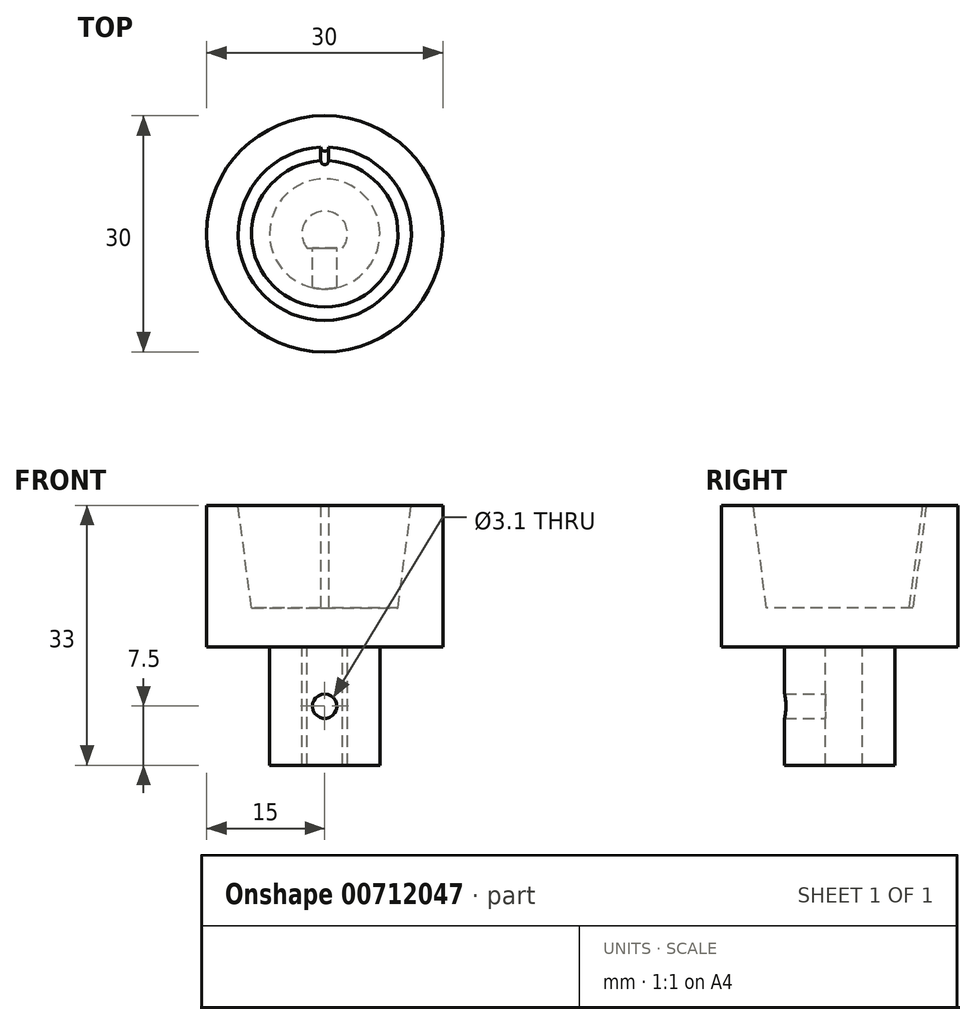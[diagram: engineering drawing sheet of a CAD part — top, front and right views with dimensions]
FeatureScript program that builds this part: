
annotation { "Feature Type Name" : "Feature", "Feature Type Description" : "" }
export const myFeature = defineFeature(function(context is Context, id is Id, definition is map)
    precondition{}
    {
        {
            var Q0;
            Q0=qCreatedBy(makeId("Top.planeOp"),FACE);
            var sketch = newSketch(context, id + "F0", { "sketchPlane" : qUnion([Q0])});
            skLineSegment(sketch, "E0", {"start": v(-2.27, -1.8) * mm, "end": v(2.27, -1.8) * mm});
            skArc(sketch, "E1", {"start": v(-2.27, -1.8) * mm, "mid": v(0, 2.9) * mm, "end": v(2.27, -1.8) * mm});
            skCircle(sketch, "E2", {"center": v(0, 0) * mm, "radius": 7 * mm});
            skCircle(sketch, "E3", {"center": v(0, 0) * mm, "radius": 10 * mm});
            skSolve(sketch);
        }
        {
            var Q0;
            Q0=makeQuery(id+"F0.imprint","IMPRINT",FACE,{"disambiguationData":[TD([[makeQuery(id+"F0.imprint","IMPRINT",EDGE,{"derivedFrom":sQuery(id+"F0.wireOp",EDGE,"E0")}),-1.0]])]});
            extrude(context, id + "F1", {"entities" : qUnion([Q0]), "oppositeDirection" : true, "depth" : 15 * mm, "offsetDistance" : 25 * mm});
        }
        {
            var Q0;
            Q0=makeQuery(id+"F0.imprint","IMPRINT",FACE,{"disambiguationData":[TD([[makeQuery(id+"F0.imprint","IMPRINT",EDGE,{"derivedFrom":sQuery(id+"F0.wireOp",EDGE,"E0")}),1.0]])]});
            var Q1;
            Q1=makeQuery(id+"F0.imprint","IMPRINT",FACE,{"disambiguationData":[TD([[makeQuery(id+"F0.imprint","IMPRINT",EDGE,{"derivedFrom":sQuery(id+"F0.wireOp",EDGE,"E0")}),-1.0]])]});
            var Q2;
            Q2=makeQuery(id+"F0.imprint","IMPRINT",FACE,{"disambiguationData":[TD([[makeQuery(id+"F0.imprint","IMPRINT",EDGE,{"derivedFrom":sQuery(id+"F0.wireOp",EDGE,"E2")}),-1.0]])]});
            extrude(context, id + "F2", {"entities" : qUnion([Q0, Q1, Q2]), "operationType" : NewBodyOperationType.ADD, "depth" : 5 * mm, "offsetDistance" : 25 * mm});
        }
        {
            var Q0;
            Q0=qCreatedBy(makeId("Right.planeOp"),FACE);
            var sketch = newSketch(context, id + "F3", { "sketchPlane" : qUnion([Q0])});
            skLineSegment(sketch, "E4", {"start": v(9.3, 0) * mm, "end": v(15, 0) * mm});
            skLineSegment(sketch, "E5", {"start": v(15, 0) * mm, "end": v(15, 18) * mm});
            skPoint(sketch, "E6.endSnap0", {"position": v(12.15, 0) * mm});
            skLineSegment(sketch, "E7", {"start": v(9.3, 5) * mm, "end": v(9.3, 0) * mm});
            skLineSegment(sketch, "E8", {"start": v(0, 0) * mm, "end": v(0, 7.26) * mm, "construction": true});
            skLineSegment(sketch, "E9", {"start": v(15, 18) * mm, "end": v(11, 18) * mm});
            skLineSegment(sketch, "E10", {"start": v(11, 18) * mm, "end": v(9.3, 5) * mm});
            skSolve(sketch);
        }
        {
            var Q0;
            Q0=makeQuery(id+"F3.imprint","IMPRINT",FACE,{"disambiguationData":[TD([[makeQuery(id+"F3.imprint","IMPRINT",EDGE,{"derivedFrom":sQuery(id+"F3.wireOp",EDGE,"E4")}),1.0]])]});
            var Q1;
            Q1=sQuery(id+"F3.wireOp",EDGE,"E8");
            revolve(context, id + "F4", {"operationType" : NewBodyOperationType.ADD, "surfaceOperationType" : NewSurfaceOperationType.NEW, "entities" : qUnion([Q0]), "axis" : qUnion([Q1]), "revolveType" : RevolveType.FULL});
        }
        {
            var Q0;
            Q0=makeQuery(id+"F1.opExtrude","SWEPT_FACE",FACE,{"disambiguationData":[OSD([sQuery(id+"F0.wireOp",EDGE,"E0")])]});
            var sketch = newSketch(context, id + "F5", { "sketchPlane" : qUnion([Q0])});
            skPoint(sketch, "E11", {"position": v(0, -7.5) * mm});
            skPoint(sketch, "E11.positionSnap0", {"position": v(0, -15) * mm});
            skSolve(sketch);
        }
        {
            var Q0;
            Q0=sQuery(id+"F5.wireOp",VERTEX,"E11");
            var Q1;
            Q1=makeQuery(id+"F1.opExtrude","SWEPT_BODY",BODY,{"disambiguationData":[OSD([sQuery(id+"F0.wireOp",EDGE,"E0"),sQuery(id+"F0.wireOp",EDGE,"E1"),sQuery(id+"F0.wireOp",EDGE,"E2")])]});
            hole(context, id + "F6", {"style" : HoleStyle.SIMPLE, "endStyle" : HoleEndStyle.THROUGH, "holeDiameter" : 3.1 * mm, "majorDiameter" : 5 * mm, "isTappedThrough" : true, "tappedDepth" : 12 * mm, "tapClearance" : 3, "locations" : qUnion([Q0]), "scope" : qUnion([Q1])});
        }
        {
            var Q0;
            Q0=makeQuery(id+"F2.opExtrude","CAP_FACE",FACE,{"disambiguationData":[OSD([sQuery(id+"F0.wireOp",EDGE,"E3")])],"isStart":false});
            var sketch = newSketch(context, id + "F7", { "sketchPlane" : qUnion([Q0])});
            skArc(sketch, "E12", {"start": v(-0.5, 9.29) * mm, "mid": v(0, 8.8) * mm, "end": v(0.5, 9.29) * mm});
            skSolve(sketch);
        }
        {
            var Q0;
            Q0=makeQuery(id+"F4.opRevolve","SWEPT_FACE",FACE,{"disambiguationData":[OSD([sQuery(id+"F3.wireOp",EDGE,"E9")])]});
            var sketch = newSketch(context, id + "F8", { "sketchPlane" : qUnion([Q0])});
            skArc(sketch, "E13", {"start": v(-0.5, 10.99) * mm, "mid": v(0, 10.5) * mm, "end": v(0.5, 10.99) * mm});
            skSolve(sketch);
        }
        {
            var Q1;
            {var subQ0=sQuery(id+"F8.wireOp",EDGE,"E13");Q1=makeQuery(id+"F8.imprint","IMPRINT",FACE,{"disambiguationData":[TD([[makeQuery(id+"F8.imprint","IMPRINT",EDGE,{"derivedFrom":subQ0}),1.0]])]});}
            var Q2;
            {var subQ0=sQuery(id+"F7.wireOp",EDGE,"E12");Q2=makeQuery(id+"F7.imprint","IMPRINT",FACE,{"disambiguationData":[TD([[makeQuery(id+"F7.imprint","IMPRINT",EDGE,{"derivedFrom":subQ0}),1.0]])]});}
            loft(context, id + "F9", {"operationType" : NewBodyOperationType.ADD, "sheetProfilesArray" : [{ "sheetProfileEntities" : qUnion([Q1]) }, { "sheetProfileEntities" : qUnion([Q2]) }]});
        }
    });
